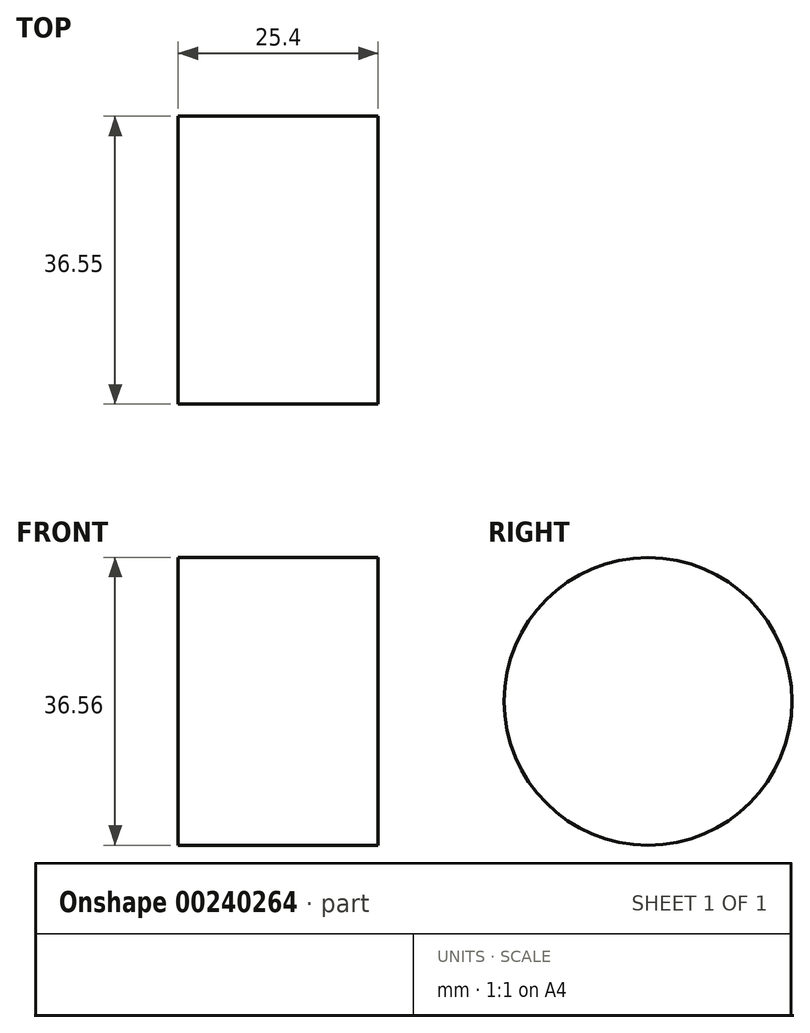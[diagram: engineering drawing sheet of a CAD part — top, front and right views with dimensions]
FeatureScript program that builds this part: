
annotation { "Feature Type Name" : "Feature", "Feature Type Description" : "" }
export const myFeature = defineFeature(function(context is Context, id is Id, definition is map)
    precondition{}
    {
        {
            var Q0;
            Q0=qCreatedBy(makeId("Right.planeOp"),FACE);
            var sketch = newSketch(context, id + "F0", { "sketchPlane" : qUnion([Q0])});
            skCircle(sketch, "E0", {"center": v(-36.38, 26.85) * mm, "radius": 18.28 * mm});
            skSolve(sketch);
        }
        {
            var Q0;
            Q0=sQuery(id+"F0.wireOp",EDGE,"E0");
            extrude(context, id + "F1", {"bodyType" : ToolBodyType.SURFACE, "surfaceEntities" : qUnion([Q0]), "depth" : 25.4 * mm});
        }
    });
